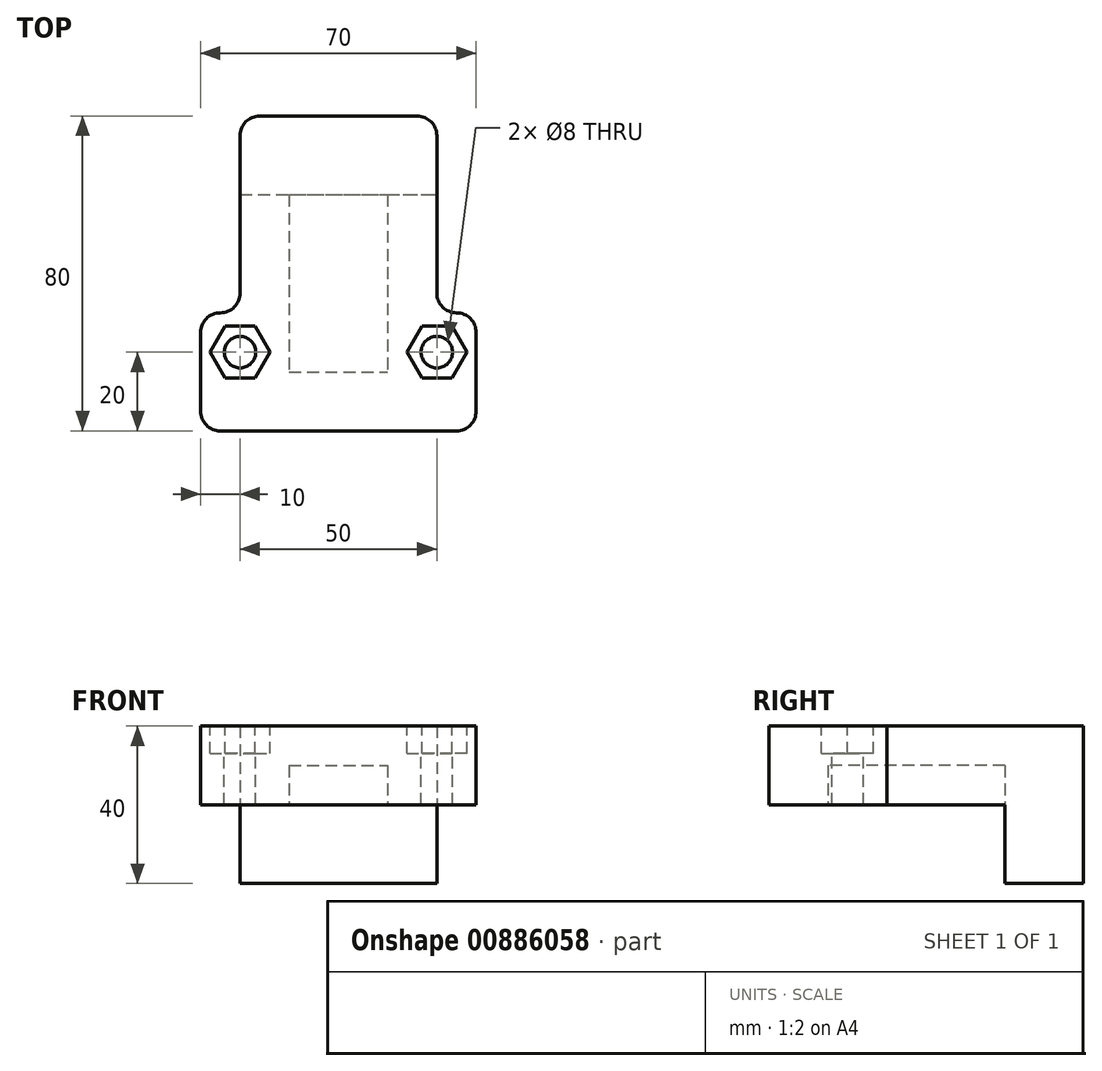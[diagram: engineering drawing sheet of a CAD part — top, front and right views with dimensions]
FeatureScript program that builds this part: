
annotation { "Feature Type Name" : "Feature", "Feature Type Description" : "" }
export const myFeature = defineFeature(function(context is Context, id is Id, definition is map)
    precondition{}
    {
        {
            var Q0;
            Q0=qCreatedBy(makeId("Top.planeOp"),FACE);
            var sketch = newSketch(context, id + "F0", { "sketchPlane" : qUnion([Q0])});
            skLineSegment(sketch, "E0.bottom", {"start": v(0, 0) * mm, "end": v(70, 0) * mm});
            skLineSegment(sketch, "E0.top", {"start": v(0, 30) * mm, "end": v(10, 30) * mm});
            skLineSegment(sketch, "E0.left", {"start": v(0, 0) * mm, "end": v(0, 30) * mm});
            skLineSegment(sketch, "E0.right", {"start": v(70, 0) * mm, "end": v(70, 30) * mm});
            skLineSegment(sketch, "E1", {"start": v(10, 80) * mm, "end": v(10, 30) * mm});
            skLineSegment(sketch, "E2", {"start": v(60, 80) * mm, "end": v(60, 30) * mm});
            skLineSegment(sketch, "E3", {"start": v(10, 80) * mm, "end": v(60, 80) * mm});
            skLineSegment(sketch, "E4.trimOffspring", {"start": v(60, 30) * mm, "end": v(70, 30) * mm});
            skSolve(sketch);
        }
        {
            var Q0;
            Q0=makeQuery(id+"F0.imprint","IMPRINT",FACE,{"disambiguationData":[TD([[makeQuery(id+"F0.imprint","IMPRINT",EDGE,{"derivedFrom":sQuery(id+"F0.wireOp",EDGE,"E0.bottom")}),1.0]])]});
            extrude(context, id + "F1", {"entities" : qUnion([Q0]), "depth" : 20 * mm, "offsetDistance" : 25 * mm});
        }
        {
            var Q0;
            Q0=makeQuery(id+"F1.opExtrude","CAP_FACE",FACE,{"disambiguationData":[OSD([sQuery(id+"F0.wireOp",EDGE,"E0.bottom"),sQuery(id+"F0.wireOp",EDGE,"E0.top"),sQuery(id+"F0.wireOp",EDGE,"E0.left"),sQuery(id+"F0.wireOp",EDGE,"E0.right"),sQuery(id+"F0.wireOp",EDGE,"E1"),sQuery(id+"F0.wireOp",EDGE,"E2"),sQuery(id+"F0.wireOp",EDGE,"E3"),sQuery(id+"F0.wireOp",EDGE,"E4.trimOffspring")])],"isStart":false});
            var sketch = newSketch(context, id + "F2", { "sketchPlane" : qUnion([Q0])});
            skCircle(sketch, "E5.cCircle", {"center": v(10, 20) * mm, "radius": 6.6 * mm, "construction": true});
            skLineSegment(sketch, "E5.0", {"start": v(13.81, 26.6) * mm, "end": v(17.62, 20) * mm});
            skLineSegment(sketch, "E5.1", {"start": v(17.62, 20) * mm, "end": v(13.81, 13.4) * mm});
            skLineSegment(sketch, "E5.2", {"start": v(13.81, 13.4) * mm, "end": v(6.19, 13.4) * mm});
            skLineSegment(sketch, "E5.3", {"start": v(6.19, 13.4) * mm, "end": v(2.38, 20) * mm});
            skLineSegment(sketch, "E5.4", {"start": v(2.38, 20) * mm, "end": v(6.19, 26.6) * mm});
            skLineSegment(sketch, "E5.5", {"start": v(6.19, 26.6) * mm, "end": v(13.81, 26.6) * mm});
            skPoint(sketch, "E5.0.midPoint", {"position": v(15.72, 23.3) * mm});
            skCircle(sketch, "E6.cCircle", {"center": v(60, 20) * mm, "radius": 6.6 * mm, "construction": true});
            skLineSegment(sketch, "E6.0", {"start": v(67.62, 20) * mm, "end": v(63.81, 13.4) * mm});
            skLineSegment(sketch, "E6.1", {"start": v(63.81, 13.4) * mm, "end": v(56.19, 13.4) * mm});
            skLineSegment(sketch, "E6.2", {"start": v(56.19, 13.4) * mm, "end": v(52.38, 20) * mm});
            skLineSegment(sketch, "E6.3", {"start": v(52.38, 20) * mm, "end": v(56.19, 26.6) * mm});
            skLineSegment(sketch, "E6.4", {"start": v(56.19, 26.6) * mm, "end": v(63.81, 26.6) * mm});
            skLineSegment(sketch, "E6.5", {"start": v(63.81, 26.6) * mm, "end": v(67.62, 20) * mm});
            skPoint(sketch, "E6.0.midPoint", {"position": v(65.72, 16.7) * mm});
            skSolve(sketch);
        }
        {
            var Q0;
            Q0=makeQuery(id+"F2.imprint","IMPRINT",FACE,{"disambiguationData":[TD([[makeQuery(id+"F2.imprint","IMPRINT",EDGE,{"derivedFrom":sQuery(id+"F2.wireOp",EDGE,"E6.0")}),-1.0]])]});
            var Q1;
            Q1=makeQuery(id+"F2.imprint","IMPRINT",FACE,{"disambiguationData":[TD([[makeQuery(id+"F2.imprint","IMPRINT",EDGE,{"derivedFrom":sQuery(id+"F2.wireOp",EDGE,"E5.0")}),-1.0]])]});
            extrude(context, id + "F3", {"entities" : qUnion([Q0, Q1]), "operationType" : NewBodyOperationType.REMOVE, "oppositeDirection" : true, "depth" : 7 * mm, "offsetDistance" : 25 * mm});
        }
        {
            var Q0;
            Q0=makeQuery(id+"F3.boolean.opBoolean","COPY",FACE,{"derivedFrom":makeQuery(id+"F3.opExtrude","CAP_FACE",FACE,{"disambiguationData":[OSD([sQuery(id+"F2.wireOp",EDGE,"E5.0"),sQuery(id+"F2.wireOp",EDGE,"E5.1"),sQuery(id+"F2.wireOp",EDGE,"E5.2"),sQuery(id+"F2.wireOp",EDGE,"E5.3"),sQuery(id+"F2.wireOp",EDGE,"E5.4"),sQuery(id+"F2.wireOp",EDGE,"E5.5")])],"isStart":false})});
            var sketch = newSketch(context, id + "F4", { "sketchPlane" : qUnion([Q0])});
            skCircle(sketch, "E7", {"center": v(10, 20) * mm, "radius": 4 * mm});
            skPoint(sketch, "E7.centerSnap0", {"position": v(10, 26.6) * mm});
            skSolve(sketch);
        }
        {
            var Q0;
            Q0=makeQuery(id+"F4.imprint","IMPRINT",FACE,{"disambiguationData":[TD([[makeQuery(id+"F4.imprint","IMPRINT",EDGE,{"derivedFrom":sQuery(id+"F4.wireOp",EDGE,"E7")}),1.0]])]});
            extrude(context, id + "F5", {"entities" : qUnion([Q0]), "operationType" : NewBodyOperationType.REMOVE, "endBound" : BoundingType.THROUGH_ALL, "oppositeDirection" : true, "depth" : 25 * mm, "offsetDistance" : 25 * mm});
        }
        {
            var Q0;
            Q0=makeQuery(id+"F1.opExtrude","CAP_FACE",FACE,{"disambiguationData":[OSD([sQuery(id+"F0.wireOp",EDGE,"E0.bottom"),sQuery(id+"F0.wireOp",EDGE,"E0.top"),sQuery(id+"F0.wireOp",EDGE,"E0.left"),sQuery(id+"F0.wireOp",EDGE,"E0.right"),sQuery(id+"F0.wireOp",EDGE,"E1"),sQuery(id+"F0.wireOp",EDGE,"E2"),sQuery(id+"F0.wireOp",EDGE,"E3"),sQuery(id+"F0.wireOp",EDGE,"E4.trimOffspring")])],"isStart":false});
            var sketch = newSketch(context, id + "F6", { "sketchPlane" : qUnion([Q0])});
            skCircle(sketch, "E8", {"center": v(60, 20) * mm, "radius": 4 * mm});
            skPoint(sketch, "E8.centerSnap0", {"position": v(60, 26.6) * mm});
            skSolve(sketch);
        }
        {
            var Q0;
            Q0=makeQuery(id+"F6.imprint","IMPRINT",FACE,{"disambiguationData":[TD([[makeQuery(id+"F6.imprint","IMPRINT",EDGE,{"derivedFrom":sQuery(id+"F6.wireOp",EDGE,"E8")}),1.0]])]});
            extrude(context, id + "F7", {"entities" : qUnion([Q0]), "operationType" : NewBodyOperationType.REMOVE, "endBound" : BoundingType.THROUGH_ALL, "oppositeDirection" : true, "depth" : 25 * mm, "offsetDistance" : 25 * mm});
        }
        {
            var Q0;
            Q0=makeQuery(id+"F1.opExtrude","CAP_FACE",FACE,{"disambiguationData":[OSD([sQuery(id+"F0.wireOp",EDGE,"E0.bottom"),sQuery(id+"F0.wireOp",EDGE,"E0.top"),sQuery(id+"F0.wireOp",EDGE,"E0.left"),sQuery(id+"F0.wireOp",EDGE,"E0.right"),sQuery(id+"F0.wireOp",EDGE,"E1"),sQuery(id+"F0.wireOp",EDGE,"E2"),sQuery(id+"F0.wireOp",EDGE,"E3"),sQuery(id+"F0.wireOp",EDGE,"E4.trimOffspring")])],"isStart":true});
            var sketch = newSketch(context, id + "F8", { "sketchPlane" : qUnion([Q0])});
            skLineSegment(sketch, "E9.bottom", {"start": v(10, -80) * mm, "end": v(60, -80) * mm});
            skLineSegment(sketch, "E9.top", {"start": v(10, -60) * mm, "end": v(60, -60) * mm});
            skLineSegment(sketch, "E9.left", {"start": v(10, -80) * mm, "end": v(10, -60) * mm});
            skLineSegment(sketch, "E9.right", {"start": v(60, -80) * mm, "end": v(60, -60) * mm});
            skSolve(sketch);
        }
        {
            var Q0;
            Q0 = qSketchRegion(id + "F8", true);
            extrude(context, id + "F9", {"entities" : qUnion([Q0]), "operationType" : NewBodyOperationType.ADD, "depth" : 20 * mm, "offsetDistance" : 25 * mm});
        }
        {
            var Q0;
            Q0=makeQuery(id+"F1.opExtrude","CAP_FACE",FACE,{"disambiguationData":[OSD([sQuery(id+"F0.wireOp",EDGE,"E0.bottom"),sQuery(id+"F0.wireOp",EDGE,"E0.top"),sQuery(id+"F0.wireOp",EDGE,"E0.left"),sQuery(id+"F0.wireOp",EDGE,"E0.right"),sQuery(id+"F0.wireOp",EDGE,"E1"),sQuery(id+"F0.wireOp",EDGE,"E2"),sQuery(id+"F0.wireOp",EDGE,"E3"),sQuery(id+"F0.wireOp",EDGE,"E4.trimOffspring")])],"isStart":true});
            var sketch = newSketch(context, id + "F10", { "sketchPlane" : qUnion([Q0])});
            skLineSegment(sketch, "E10.bottom", {"start": v(22.5, -60) * mm, "end": v(47.5, -60) * mm});
            skLineSegment(sketch, "E10.top", {"start": v(22.5, -15) * mm, "end": v(47.5, -15) * mm});
            skLineSegment(sketch, "E10.left", {"start": v(22.5, -60) * mm, "end": v(22.5, -15) * mm});
            skLineSegment(sketch, "E10.right", {"start": v(47.5, -60) * mm, "end": v(47.5, -15) * mm});
            skSolve(sketch);
        }
        {
            var Q0;
            Q0 = qSketchRegion(id + "F10", true);
            extrude(context, id + "F11", {"entities" : qUnion([Q0]), "operationType" : NewBodyOperationType.REMOVE, "oppositeDirection" : true, "depth" : 10 * mm, "offsetDistance" : 25 * mm});
        }
        {
            var Q0;
            Q0=makeQuery(id+"F9.boolean.opBoolean","MERGE",EDGE,{"derivedFrom":[makeQuery(id+"F1.opExtrude","SWEPT_EDGE",EDGE,{"disambiguationData":[OSD([sQuery(id+"F0.wireOp",EDGE,"E1"),sQuery(id+"F0.wireOp",EDGE,"E3")])]}),makeQuery(id+"F9.opExtrude","SWEPT_EDGE",EDGE,{"disambiguationData":[OSD([sQuery(id+"F8.wireOp",EDGE,"E9.bottom"),sQuery(id+"F8.wireOp",EDGE,"E9.left")])]})]});
            var Q1;
            Q1=makeQuery(id+"F1.opExtrude","SWEPT_EDGE",EDGE,{"disambiguationData":[OSD([sQuery(id+"F0.wireOp",EDGE,"E0.top"),sQuery(id+"F0.wireOp",EDGE,"E1")])]});
            var Q2;
            Q2=makeQuery(id+"F1.opExtrude","SWEPT_EDGE",EDGE,{"disambiguationData":[OSD([sQuery(id+"F0.wireOp",EDGE,"E2"),sQuery(id+"F0.wireOp",EDGE,"E4.trimOffspring")])]});
            var Q3;
            Q3=makeQuery(id+"F1.opExtrude","SWEPT_EDGE",EDGE,{"disambiguationData":[OSD([sQuery(id+"F0.wireOp",EDGE,"E0.right"),sQuery(id+"F0.wireOp",EDGE,"E4.trimOffspring")])]});
            var Q4;
            Q4=makeQuery(id+"F1.opExtrude","SWEPT_EDGE",EDGE,{"disambiguationData":[OSD([sQuery(id+"F0.wireOp",EDGE,"E0.bottom"),sQuery(id+"F0.wireOp",EDGE,"E0.right")])]});
            var Q5;
            Q5=makeQuery(id+"F1.opExtrude","SWEPT_EDGE",EDGE,{"disambiguationData":[OSD([sQuery(id+"F0.wireOp",EDGE,"E0.bottom"),sQuery(id+"F0.wireOp",EDGE,"E0.left")])]});
            var Q6;
            Q6=makeQuery(id+"F1.opExtrude","SWEPT_EDGE",EDGE,{"disambiguationData":[OSD([sQuery(id+"F0.wireOp",EDGE,"E0.top"),sQuery(id+"F0.wireOp",EDGE,"E0.left")])]});
            var Q7;
            Q7=makeQuery(id+"F9.boolean.opBoolean","MERGE",EDGE,{"derivedFrom":[makeQuery(id+"F1.opExtrude","SWEPT_EDGE",EDGE,{"disambiguationData":[OSD([sQuery(id+"F0.wireOp",EDGE,"E2"),sQuery(id+"F0.wireOp",EDGE,"E3")])]}),makeQuery(id+"F9.opExtrude","SWEPT_EDGE",EDGE,{"disambiguationData":[OSD([sQuery(id+"F8.wireOp",EDGE,"E9.bottom"),sQuery(id+"F8.wireOp",EDGE,"E9.right")])]})]});
            fillet(context, id + "F12", {"entities" : qUnion([Q0, Q1, Q2, Q3, Q4, Q5, Q6, Q7]), "radius" : 5 * mm, "tangentPropagation" : true, "allowEdgeOverflow" : false});
        }
    });
